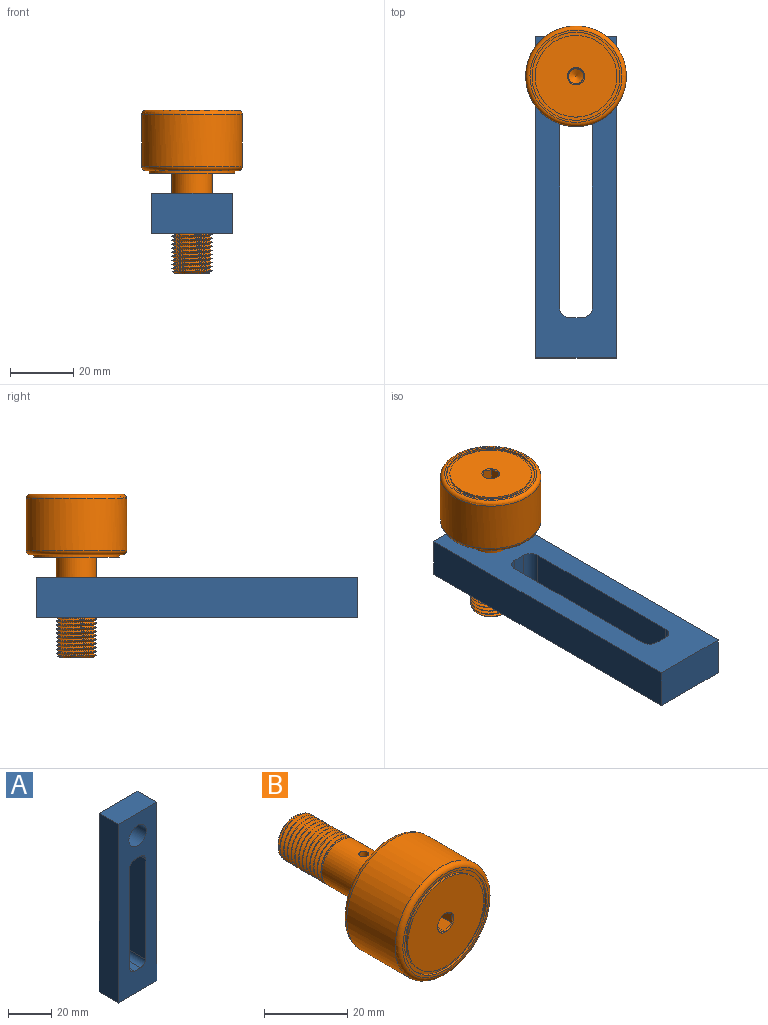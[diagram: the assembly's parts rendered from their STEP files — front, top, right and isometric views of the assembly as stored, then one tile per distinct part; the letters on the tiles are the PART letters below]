
ASSEMBLY  parts=2 mates=1
PART A: 15 faces, bbox 25.4x12.7x101.6 mm
  f0: cylinder r=3.17mm len=12.7mm, axis (0,1,0), area 63.3mm2, adj f1,f11,f12,f13
  f1: plane 57.15x12.7mm, normal (-1,0,0), area 725.8mm2, adj f0,f2,f12,f13
  f2: cylinder r=3.17mm len=12.7mm, axis (0,1,0), area 63.3mm2, adj f1,f3,f12,f13
  f3: plane 12.7x3.97mm, normal (0,0,1), area 50.4mm2, adj f2,f4,f12,f13
  f4: cylinder r=3.17mm len=12.7mm, axis (0,1,0), area 63.3mm2, adj f3,f5,f12,f13
  f5: plane 57.15x12.7mm, normal (1,0,0), area 725.8mm2, adj f4,f6,f12,f13
  f6: cylinder r=3.17mm len=12.7mm, axis (0,1,0), area 63.3mm2, adj f5,f11,f12,f13
  f7: plane 101.6x12.7mm, normal (-1,0,0), area 1290.3mm2, adj f8,f10,f12,f13
  f8: plane 25.4x12.7mm, normal (0,0,-1), area 322.6mm2, adj f7,f9,f12,f13
  f9: plane 101.6x12.7mm, normal (1,0,0), area 1290.3mm2, adj f8,f10,f12,f13
  f10: plane 25.4x12.7mm, normal (0,0,1), area 322.6mm2, adj f7,f9,f12,f13
  f11: plane 12.7x3.97mm, normal (0,0,-1), area 50.4mm2, adj f0,f6,f12,f13
  f12: plane 101.6x25.4mm, normal (0,-1,0), area 1830mm2, adj f0,f1,f2,f3,f4,f5,f6,f7
  f13: plane 101.6x25.4mm, normal (0,1,0), area 1830mm2, adj f0,f1,f2,f3,f4,f5,f6,f7
  f14: cylinder r=5.75mm len=12.7mm, axis (0,1,0), area 459.2mm2, adj f12,f13
PART B: 52 faces, bbox 35.4x53.1x35.4 mm
  f0: cylinder r=6.35mm len=16.51mm, axis (0,1,0), area 631.7mm2, adj f12,f24,f26,f28,f29,f51
  f1: cylinder r=6.35mm len=10.84mm, axis (0,1,0), area 2mm2, adj f2,f19,f26,f28
  f2: cylinder r=6.35mm len=12.7mm, axis (0,1,0), area 6.3mm2, adj f1,f3,f26,f28
  f3: cylinder r=6.35mm len=12.7mm, axis (0,1,0), area 6.3mm2, adj f2,f4,f26,f28
  f4: cylinder r=6.35mm len=12.7mm, axis (0,1,0), area 6.3mm2, adj f3,f5,f26,f28
  f5: cylinder r=6.35mm len=12.7mm, axis (0,1,0), area 6.3mm2, adj f4,f6,f26,f28
  f6: cylinder r=6.35mm len=12.7mm, axis (0,1,0), area 6.3mm2, adj f5,f7,f26,f28
  f7: cylinder r=6.35mm len=12.7mm, axis (0,1,0), area 6.3mm2, adj f6,f8,f26,f28
  f8: cylinder r=6.35mm len=12.7mm, axis (0,1,0), area 6.3mm2, adj f7,f9,f26,f28
  f9: cylinder r=6.35mm len=12.7mm, axis (0,1,0), area 6.3mm2, adj f8,f10,f26,f28
  f10: cylinder r=6.35mm len=12.7mm, axis (0,1,0), area 6.3mm2, adj f9,f11,f26,f28
  f11: cylinder r=6.35mm len=12.7mm, axis (0,1,0), area 6.3mm2, adj f10,f12,f26,f28
  f12: cylinder r=6.35mm len=12.7mm, axis (0,1,0), area 6.3mm2, adj f0,f11,f26,f28
  f13: plane 2.06x1.19mm, normal (0,-1,0), area 0.3mm2, adj f43,f44,f47
  f14: plane 2.38x0.69mm, normal (0,-1,0), area 0.3mm2, adj f44,f45,f47
  f15: plane 2.06x1.19mm, normal (0,-1,0), area 0.3mm2, adj f45,f46,f47
  f16: plane 2.06x1.19mm, normal (0,-1,0), area 0.3mm2, adj f41,f46,f47
  f17: plane 2.38x0.69mm, normal (0,-1,0), area 0.3mm2, adj f41,f42,f47
  f18: cone r=5.4mm half-angle=45deg, axis (0,-1,0), area 21.9mm2, adj f19,f25,f26,f27
  f19: cone r=5.4mm half-angle=45deg, axis (0,-1,0), area 5.6mm2, adj f1,f18,f26,f28
  f20: plane 29.08x29.08mm, normal (0,-1,0), area 58.1mm2, adj f30,f49
  f21: cylinder r=15.88mm len=31.75mm, axis (0,1,0), area 1634.1mm2, adj f48,f49
  f22: plane 29.08x29.08mm, normal (0,1,0), area 92.3mm2, adj f23,f48
  f23: cylinder r=13.49mm len=26.99mm, axis (0,1,0), area 67.3mm2, adj f22,f24
  f24: plane 26.99x26.99mm, normal (0,1,0), area 445.3mm2, adj f0,f23
  f25: plane 10.8x10.8mm, normal (0,1,0), area 91.5mm2, adj f18
  f26: bspline ~16.83x12.7mm, area 428.9mm2, adj f0,f1,f2,f3,f4,f5,f6,f7
  f27: cylinder r=5.53mm len=15.75mm, axis (0,1,0), area 67.9mm2, adj f18,f26,f28,f29
  f28: bspline ~16.35x12.7mm, area 428mm2, adj f0,f1,f2,f3,f4,f5,f6,f7
  f29: plane 13.21x13.21mm, normal (0,1,0), area 15.7mm2, adj f0,f26,f27,f28
  f30: cylinder r=13.89mm len=27.78mm, axis (0,-1,0), area 49.9mm2, adj f20,f31
  f31: plane 27.78x27.78mm, normal (0,-1,0), area 83.5mm2, adj f30,f32
  f32: cylinder r=12.9mm len=25.8mm, axis (0,-1,0), area 46.3mm2, adj f31,f33
  f33: plane 25.8x25.8mm, normal (0,-1,0), area 498.9mm2, adj f32,f34,f35,f36,f37,f38,f39
  f34: cone r=2.75mm half-angle=45deg, axis (0,-1,0), area 0mm2, adj f33,f41
  f35: cone r=2.75mm half-angle=45deg, axis (0,-1,0), area 0mm2, adj f33,f42
  f36: cone r=2.75mm half-angle=45deg, axis (0,-1,0), area 0mm2, adj f33,f43
  f37: cone r=2.75mm half-angle=45deg, axis (0,-1,0), area 0mm2, adj f33,f44
  f38: cone r=2.75mm half-angle=45deg, axis (0,-1,0), area 0mm2, adj f33,f45
  f39: cone r=2.75mm half-angle=45deg, axis (0,-1,0), area 0mm2, adj f33,f46
  f40: plane 2.06x1.19mm, normal (0,-1,0), area 0.3mm2, adj f42,f43,f47
  f41: plane 5.49x3.42mm, normal (0.5,0,0.87), area 11.6mm2, adj f16,f17,f34,f42,f46
  f42: plane 5.49x3.42mm, normal (-0.5,0,0.87), area 11.6mm2, adj f17,f35,f40,f41,f43
  f43: plane 5.49x3.8mm, normal (-1,0,0), area 11.6mm2, adj f13,f36,f40,f42,f44
  f44: plane 5.49x3.42mm, normal (-0.5,0,-0.87), area 11.6mm2, adj f13,f14,f37,f43,f45
  f45: plane 5.49x3.42mm, normal (0.5,0,-0.87), area 11.6mm2, adj f14,f15,f38,f44,f46
  f46: plane 5.49x3.8mm, normal (1,0,0), area 11.6mm2, adj f15,f16,f39,f41,f45
  f47: cone r=2.38mm half-angle=60deg, axis (0,-1,0), area 20.6mm2, adj f13,f14,f15,f16,f17,f40
  f48: torus R=14.54mm, axis (0,1,0), area 202.6mm2, adj f21,f22
  f49: torus R=14.54mm, axis (0,-1,0), area 202.6mm2, adj f20,f21
  f50: cone r=0mm half-angle=60deg, axis (0,0,1), area 5.1mm2, adj f51
  f51: cylinder r=1.19mm len=3.97mm, axis (0,0,1), area 29.7mm2, adj f0,f50
PLACE A rot(axis=(-1,0,0),90deg) t=(-12.7,0,-12.7)mm
PLACE B rot(axis=(-0.99,-0.07,0.07),90.3deg) t=(0,88.9,26.19)mm
MATE revolute A.f14 <-> B.f49  axis (0,0,-1) through (0,88.9,0)mm
